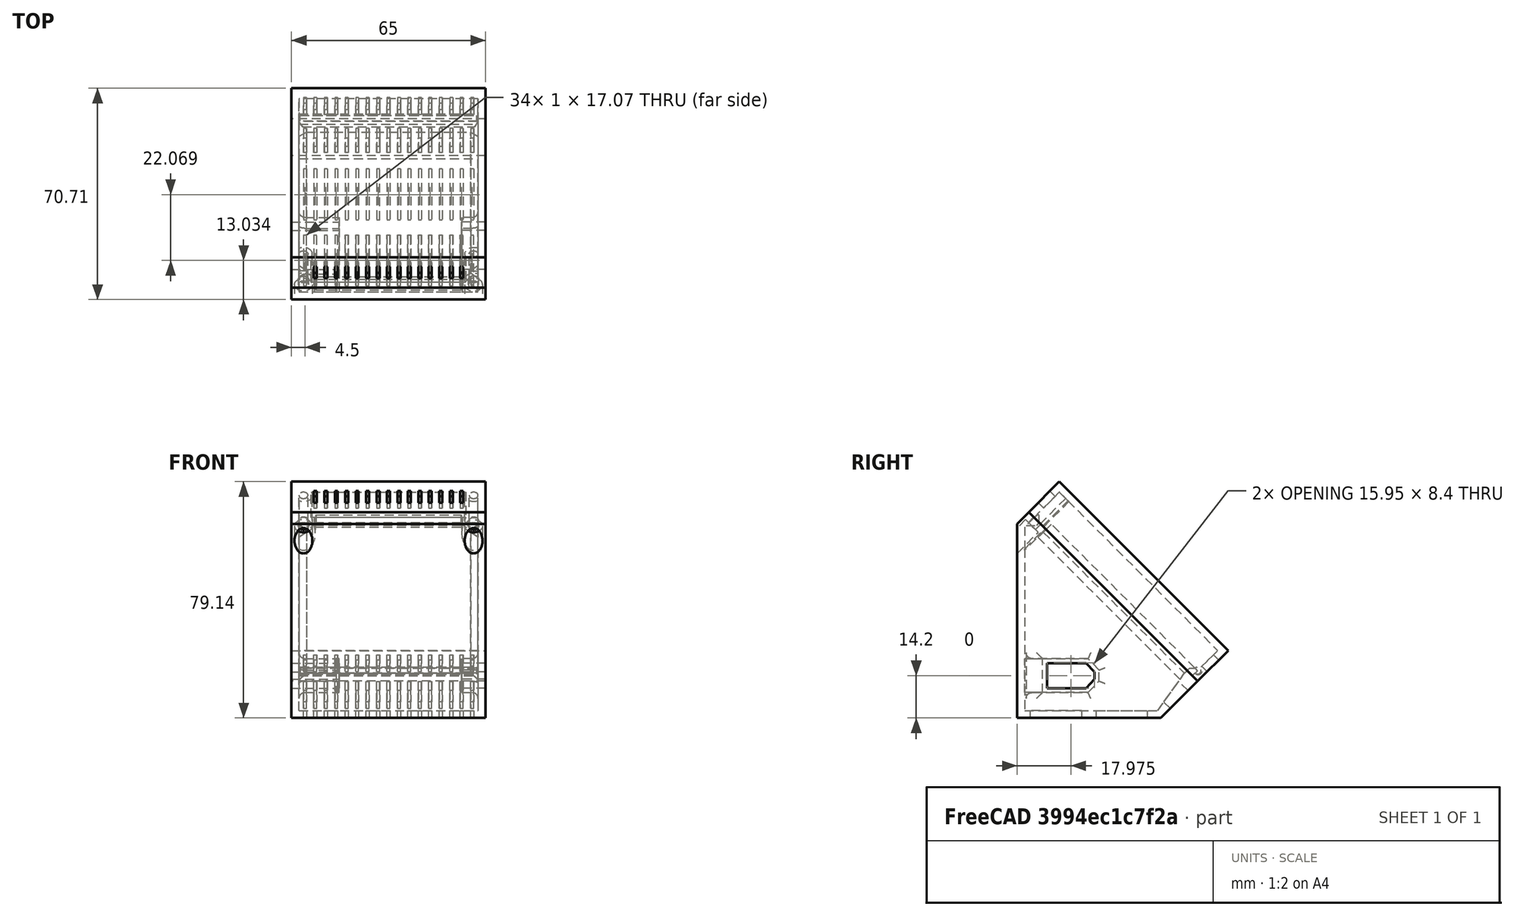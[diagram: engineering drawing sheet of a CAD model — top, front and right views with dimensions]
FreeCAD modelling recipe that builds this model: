
FCSTD DOCUMENT  (FreeCAD 0.18R4 (GitTag))
Label: templateFavSeparee
License: All rights reserved
LicenseURL: http://en.wikipedia.org/wiki/All_rights_reserved
objects: Part::Feature×2, PartDesign::FeatureBase×2, PartDesign::Body×2, App::Part×2, Sketcher::SketchObject×1
note: 7 computed .brp shape members not serialized (recipe doc carries the construction recipe); baked Part::Feature solids carry a one-line shape summary decoded from their .brp

FEATURE [Part::Feature] Part__Feature  label="Your Module"
  shape: bbox 65 x 65.85 x 68.89 mm, 287 faces (baked)
FEATURE [Part::Feature] Part__Feature001  label="Your Module001"
  shape: bbox 65 x 66.82 x 66.82 mm, 147 faces (baked)
FEATURE [PartDesign::FeatureBase] Clone
  BaseFeature = -> Part__Feature001
FEATURE [Sketcher::SketchObject] Sketch
  MapMode = 5
  Placement = pos=(0,36.3891,36.3891) rot=(1,0,0;2.35619rad)
  Support = -> [Clone]
  sketch-geometry (4):
    g0: LineSegment StartX=-32.5225 StartY=20.176 StartZ=0 EndX=-30.0362 EndY=20.176 EndZ=0
    g1: LineSegment StartX=-30.0362 StartY=20.176 StartZ=0 EndX=-30.0362 EndY=8.84985 EndZ=0
    g2: LineSegment StartX=-30.0362 StartY=8.84985 StartZ=0 EndX=-32.5225 EndY=8.84985 EndZ=0
    g3: LineSegment StartX=-32.5225 StartY=8.84985 StartZ=0 EndX=-32.5225 EndY=20.176 EndZ=0
  constraints (8):
    c: Coincident(g0,g1)
    c: Coincident(g1,g2)
    c: Coincident(g2,g3)
    c: Coincident(g3,g0)
    c: Horizontal(g0)
    c: Horizontal(g2)
    c: Vertical(g1)
    c: Vertical(g3)
FEATURE [PartDesign::Body] Body
  Group = -> [Clone,Sketch]
  Origin = -> Origin
  Tip = -> Clone
FEATURE [App::Part] Template_separe_v1001  label="Template_separe v002"
  Group = -> [Part__Feature001,Body]
  Origin = -> Origin002
  Placement = pos=(0,0,0) rot=(1,0,0;1.5708rad)
FEATURE [PartDesign::FeatureBase] Clone001
  BaseFeature = -> Part__Feature
FEATURE [PartDesign::Body] Body001
  Group = -> [Clone001]
  Origin = -> Origin003
  Tip = -> Clone001
FEATURE [App::Part] Template_separe_v1  label="Template_separe v1"
  Group = -> [Part__Feature,Body001]
  Origin = -> Origin001
  Placement = pos=(0,0,0) rot=(1,0,0;1.5708rad)
